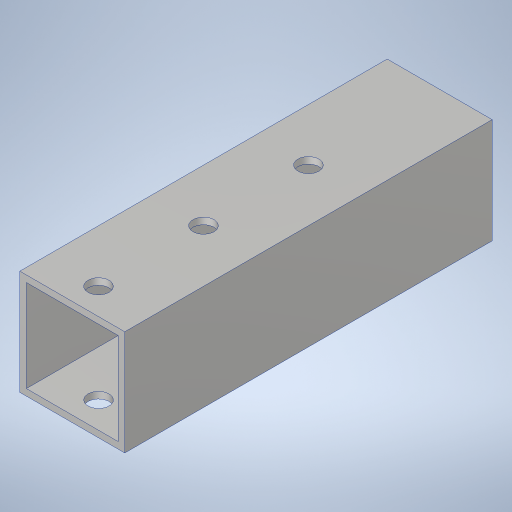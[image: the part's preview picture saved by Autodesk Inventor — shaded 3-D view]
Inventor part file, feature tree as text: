
AUTODESK INVENTOR PART (.ipt)
format: ipt  version: 2023.4 (Build 274418000, 418)  size: 215,552 bytes
history: native  units: in
note: dims shown in document units (in); Inventor stores cm internally (conversion verified against a paired STEP export)
features: sketch x2, extrude x1, hole x1
ambient origin geometry x8: Origin, YZ Plane, XZ Plane, XY Plane, X Axis, Y Axis, Z Axis, Center Point
bodies: Solid1 (feature_tree)
feature tree (4):
  extrude  "Extrusion1"  Depth=1.0in
  hole  "Hole1"  [1 undecoded]
  sketch  "Sketch1"  dims[d0=1.0in d1=1.0in]
  sketch  "Sketch2"  dims[d3=0.875in d4=0.875in d5=3.5in d6=0.0in d7=0.25in d8=1.0in d9=1.0in d10=0.201in d11=0.75in d12=0.385in d13=0.25in d14=0.5635in d15=1.0in d16=0.8108in]
note: 1 required parameter value undecoded (feature->parameter linkage not recoverable at this tier; creation-order binding heuristic only, values carry confidence <= 0.55)
